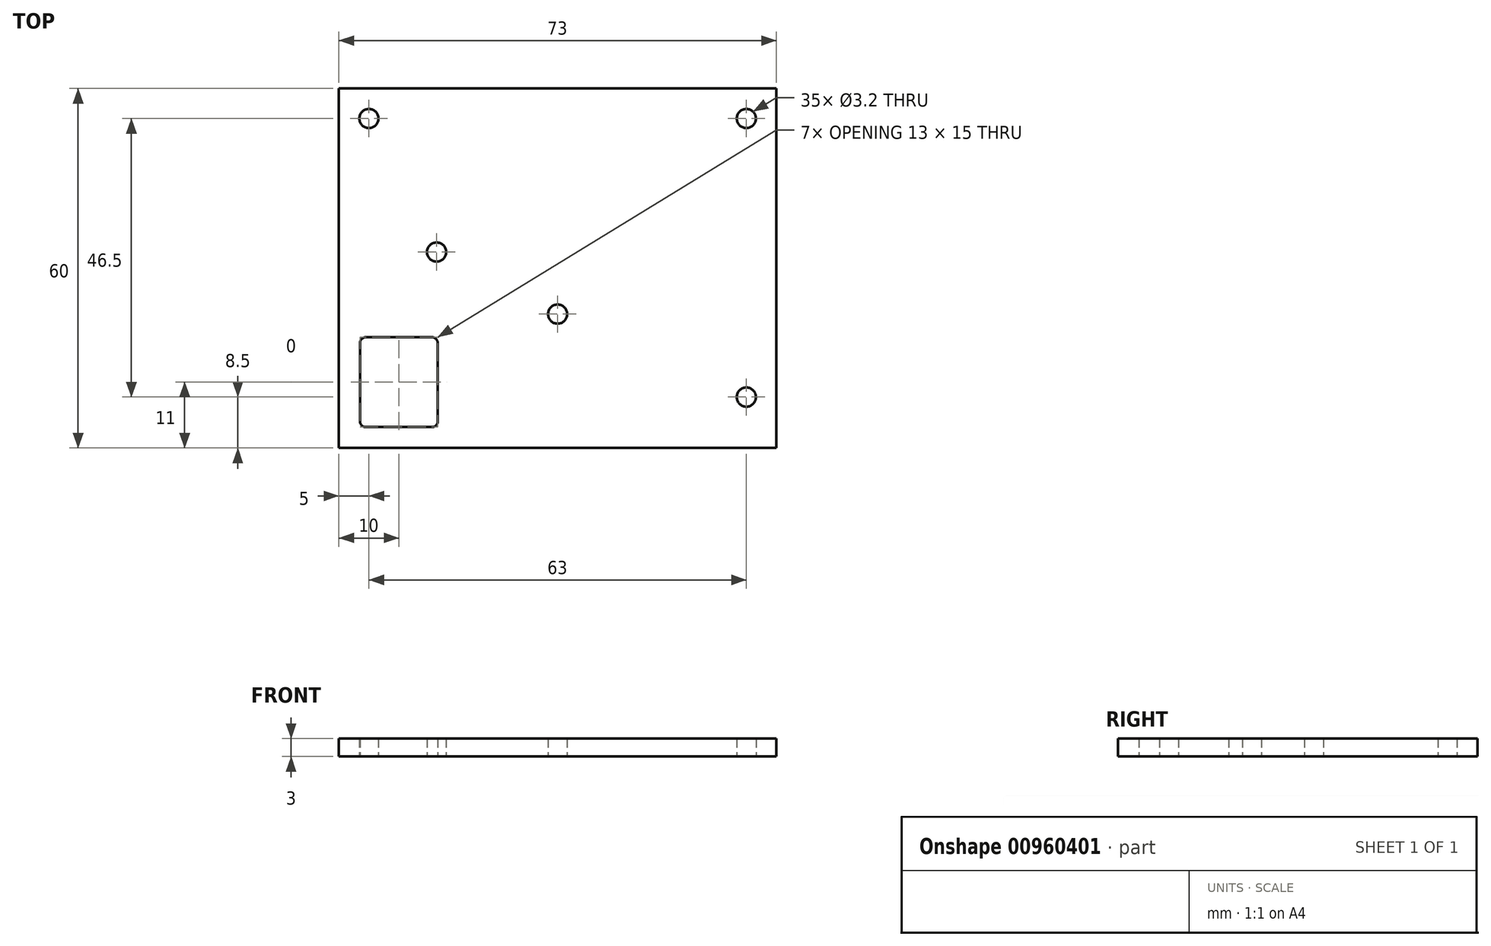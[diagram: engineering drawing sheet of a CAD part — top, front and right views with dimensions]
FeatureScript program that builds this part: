
annotation { "Feature Type Name" : "Feature", "Feature Type Description" : "" }
export const myFeature = defineFeature(function(context is Context, id is Id, definition is map)
    precondition{}
    {
        {
            var Q0;
            Q0=qCreatedBy(makeId("Top.planeOp"),FACE);
            var sketch = newSketch(context, id + "F0", { "sketchPlane" : qUnion([Q0])});
            skLineSegment(sketch, "E0.bottom", {"start": v(-73, -60) * mm, "end": v(0, -60) * mm});
            skLineSegment(sketch, "E0.top", {"start": v(-73, 0) * mm, "end": v(0, 0) * mm});
            skLineSegment(sketch, "E0.left", {"start": v(-73, -60) * mm, "end": v(-73, 0) * mm});
            skLineSegment(sketch, "E0.right", {"start": v(0, -60) * mm, "end": v(0, 0) * mm});
            skCircle(sketch, "E1", {"center": v(-56.7, -27.3) * mm, "radius": 1.6 * mm});
            skCircle(sketch, "E2", {"center": v(-36.5, -37.65) * mm, "radius": 1.6 * mm});
            skCircle(sketch, "E3", {"center": v(-36.5, -37.65) * mm, "radius": 18.35 * mm, "construction": true});
            skCircle(sketch, "E4", {"center": v(-56.7, -27.3) * mm, "radius": 18.35 * mm, "construction": true});
            skCircle(sketch, "E5", {"center": v(-56.7, -27.3) * mm, "radius": 4.35 * mm, "construction": true});
            skCircle(sketch, "E6", {"center": v(-63, -49) * mm, "radius": 4.25 * mm, "construction": true});
            skLineSegment(sketch, "E7.bottom", {"start": v(-69.5, -56.5) * mm, "end": v(-56.5, -56.5) * mm});
            skLineSegment(sketch, "E7.top", {"start": v(-69.5, -41.5) * mm, "end": v(-56.5, -41.5) * mm});
            skLineSegment(sketch, "E7.left", {"start": v(-69.5, -56.5) * mm, "end": v(-69.5, -41.5) * mm});
            skLineSegment(sketch, "E7.right", {"start": v(-56.5, -56.5) * mm, "end": v(-56.5, -41.5) * mm});
            skLineSegment(sketch, "E8", {"start": v(-69.5, -41.5) * mm, "end": v(-56.5, -56.5) * mm, "construction": true});
            skCircle(sketch, "E9", {"center": v(-68, -5) * mm, "radius": 1.6 * mm});
            skCircle(sketch, "E10", {"center": v(-5, -5) * mm, "radius": 1.6 * mm});
            skCircle(sketch, "E11", {"center": v(-5, -51.5) * mm, "radius": 1.6 * mm});
            skLineSegment(sketch, "E12", {"start": v(-73, -37.65) * mm, "end": v(0, -37.65) * mm, "construction": true});
            skPoint(sketch, "E13", {"position": v(0, -30) * mm});
            skSolve(sketch);
        }
        {
            var Q0;
            Q0=qSketchRegion(id+"F0",true);
            extrude(context, id + "F1", {"entities" : qUnion([Q0]), "depth" : 3 * mm, "offsetDistance" : 25 * mm});
        }
        {
            var Q0;
            Q0=makeQuery(id+"F1.opExtrude","SWEPT_EDGE",EDGE,{"disambiguationData":[OSD([sQuery(id+"F0.wireOp",EDGE,"E7.top"),sQuery(id+"F0.wireOp",EDGE,"E7.left")])]});
            var Q1;
            Q1=makeQuery(id+"F1.opExtrude","SWEPT_EDGE",EDGE,{"disambiguationData":[OSD([sQuery(id+"F0.wireOp",EDGE,"E7.bottom"),sQuery(id+"F0.wireOp",EDGE,"E7.right")])]});
            var Q2;
            Q2=makeQuery(id+"F1.opExtrude","SWEPT_EDGE",EDGE,{"disambiguationData":[OSD([sQuery(id+"F0.wireOp",EDGE,"E7.bottom"),sQuery(id+"F0.wireOp",EDGE,"E7.left")])]});
            var Q3;
            Q3=makeQuery(id+"F1.opExtrude","SWEPT_EDGE",EDGE,{"disambiguationData":[OSD([sQuery(id+"F0.wireOp",EDGE,"E7.top"),sQuery(id+"F0.wireOp",EDGE,"E7.right")])]});
            fillet(context, id + "F2", {"entities" : qUnion([Q0, Q1, Q2, Q3]), "radius" : 1 * mm, "tangentPropagation" : true, "allowEdgeOverflow" : false});
        }
    });
